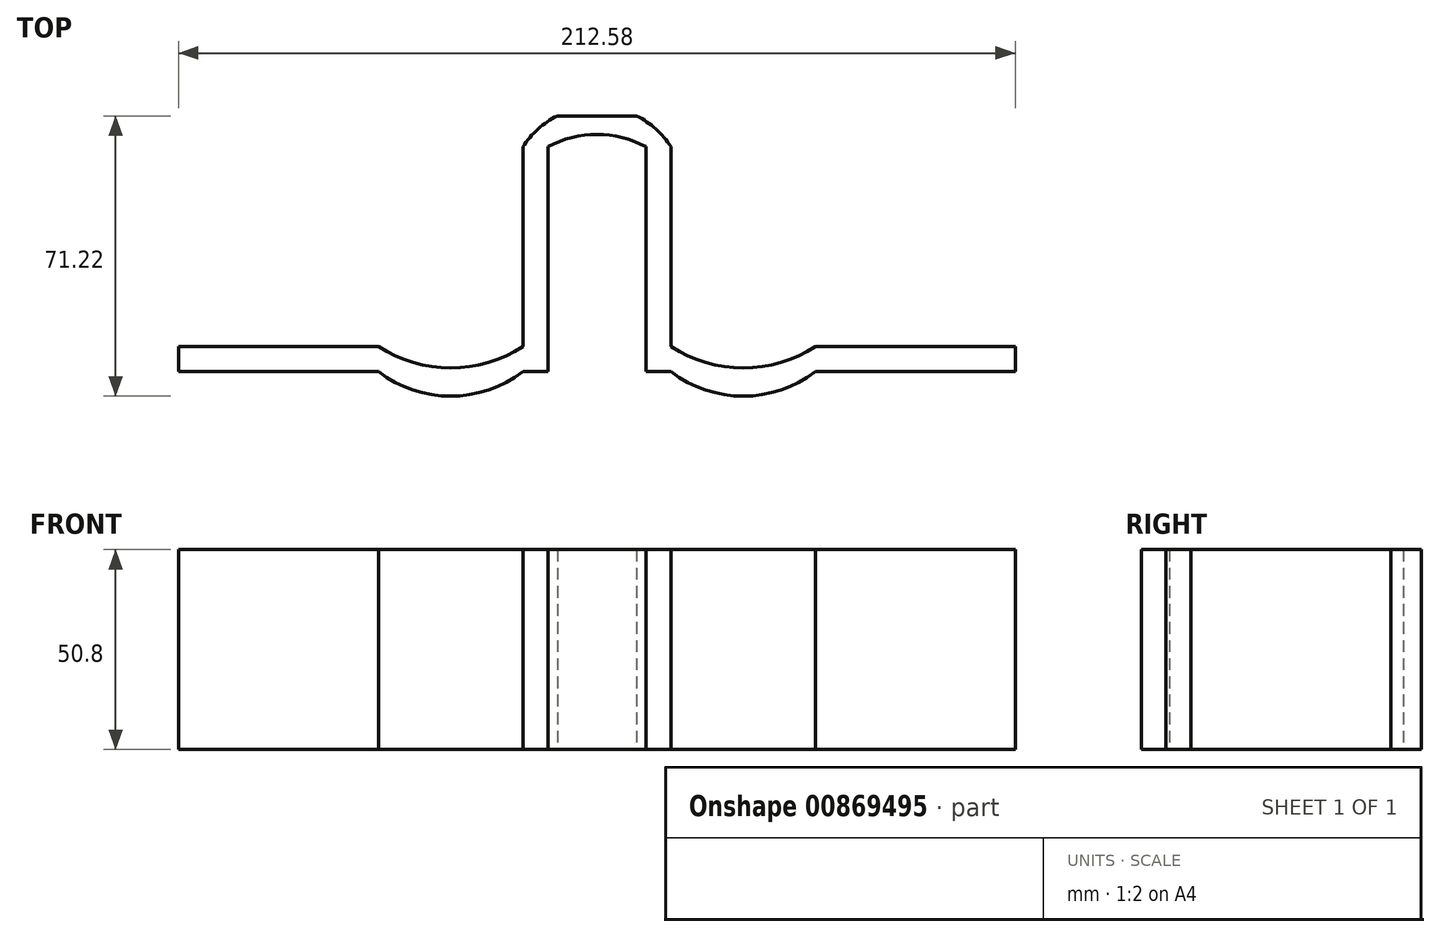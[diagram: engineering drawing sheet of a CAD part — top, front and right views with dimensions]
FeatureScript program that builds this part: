
annotation { "Feature Type Name" : "Feature", "Feature Type Description" : "" }
export const myFeature = defineFeature(function(context is Context, id is Id, definition is map)
    precondition{}
    {
        {
            var Q0;
            Q0=qCreatedBy(makeId("Top.planeOp"),FACE);
            var sketch = newSketch(context, id + "F0", { "sketchPlane" : qUnion([Q0])});
            skLineSegment(sketch, "E0", {"start": v(-109.6, 0) * mm, "end": v(-58.8, 0) * mm});
            skLineSegment(sketch, "E1", {"start": v(-109.6, 0) * mm, "end": v(-109.6, -6.35) * mm});
            skLineSegment(sketch, "E2", {"start": v(-109.6, -6.35) * mm, "end": v(-58.8, -6.35) * mm});
            skArc(sketch, "E3", {"start": v(-58.8, 0) * mm, "mid": v(-40.46, -5.4) * mm, "end": v(-22.12, 0) * mm});
            skArc(sketch, "E4", {"start": v(-58.8, -6.35) * mm, "mid": v(-40.46, -12.56) * mm, "end": v(-22.12, -6.35) * mm});
            skPoint(sketch, "E5.end.orphan", {"position": v(-40.46, 43.91) * mm});
            skLineSegment(sketch, "E6", {"start": v(-22.12, 0) * mm, "end": v(-22.12, 50.8) * mm});
            skLineSegment(sketch, "E7", {"start": v(-22.12, -6.35) * mm, "end": v(-15.77, -6.35) * mm});
            skLineSegment(sketch, "E8", {"start": v(-15.77, -6.35) * mm, "end": v(-15.77, 50.8) * mm});
            skArc(sketch, "E9", {"start": v(-3.3, 53.95) * mm, "mid": v(-9.73, 53.15) * mm, "end": v(-15.77, 50.8) * mm});
            skLineSegment(sketch, "E10", {"start": v(-13.38, 58.66) * mm, "end": v(-3.3, 58.66) * mm});
            skArc(sketch, "E11.trimOffspring", {"start": v(-13.38, 58.66) * mm, "mid": v(-18.27, 55.31) * mm, "end": v(-22.12, 50.8) * mm});
            skPoint(sketch, "E12.orphan", {"position": v(9.18, 50.8) * mm});
            skPoint(sketch, "E13.end.orphan", {"position": v(6.78, 58.66) * mm});
            skPoint(sketch, "E13.start.orphan", {"position": v(15.53, 50.8) * mm});
            skArc(sketch, "E14.MirrorCS", {"start": v(-3.3, 53.95) * mm, "mid": v(3.13, 53.15) * mm, "end": v(9.18, 50.8) * mm});
            skLineSegment(sketch, "E15.MirrorCS", {"start": v(6.78, 58.66) * mm, "end": v(-3.3, 58.66) * mm});
            skArc(sketch, "E16.MirrorCS", {"start": v(6.78, 58.66) * mm, "mid": v(11.68, 55.31) * mm, "end": v(15.53, 50.8) * mm});
            skLineSegment(sketch, "E17.MirrorCS", {"start": v(15.53, 0) * mm, "end": v(15.53, 50.8) * mm});
            skLineSegment(sketch, "E18.MirrorCS", {"start": v(9.18, -6.35) * mm, "end": v(9.18, 50.8) * mm});
            skArc(sketch, "E19.MirrorCS", {"start": v(52.2, -6.35) * mm, "mid": v(33.86, -12.56) * mm, "end": v(15.53, -6.35) * mm});
            skArc(sketch, "E20.MirrorCS", {"start": v(52.2, 0) * mm, "mid": v(33.86, -5.4) * mm, "end": v(15.53, 0) * mm});
            skLineSegment(sketch, "E21.MirrorCS", {"start": v(103, -6.35) * mm, "end": v(52.2, -6.35) * mm});
            skLineSegment(sketch, "E22.MirrorCS", {"start": v(103, 0) * mm, "end": v(52.2, 0) * mm});
            skLineSegment(sketch, "E23.MirrorCS", {"start": v(103, 0) * mm, "end": v(103, -6.35) * mm});
            skLineSegment(sketch, "E24", {"start": v(9.18, -6.35) * mm, "end": v(15.53, -6.35) * mm});
            skSolve(sketch);
        }
        {
            var Q0;
            Q0 = qSketchRegion(id + "F0", true);
            extrude(context, id + "F1", {"entities" : qUnion([Q0]), "depth" : 50.8 * mm, "offsetDistance" : 25.4 * mm});
        }
    });
